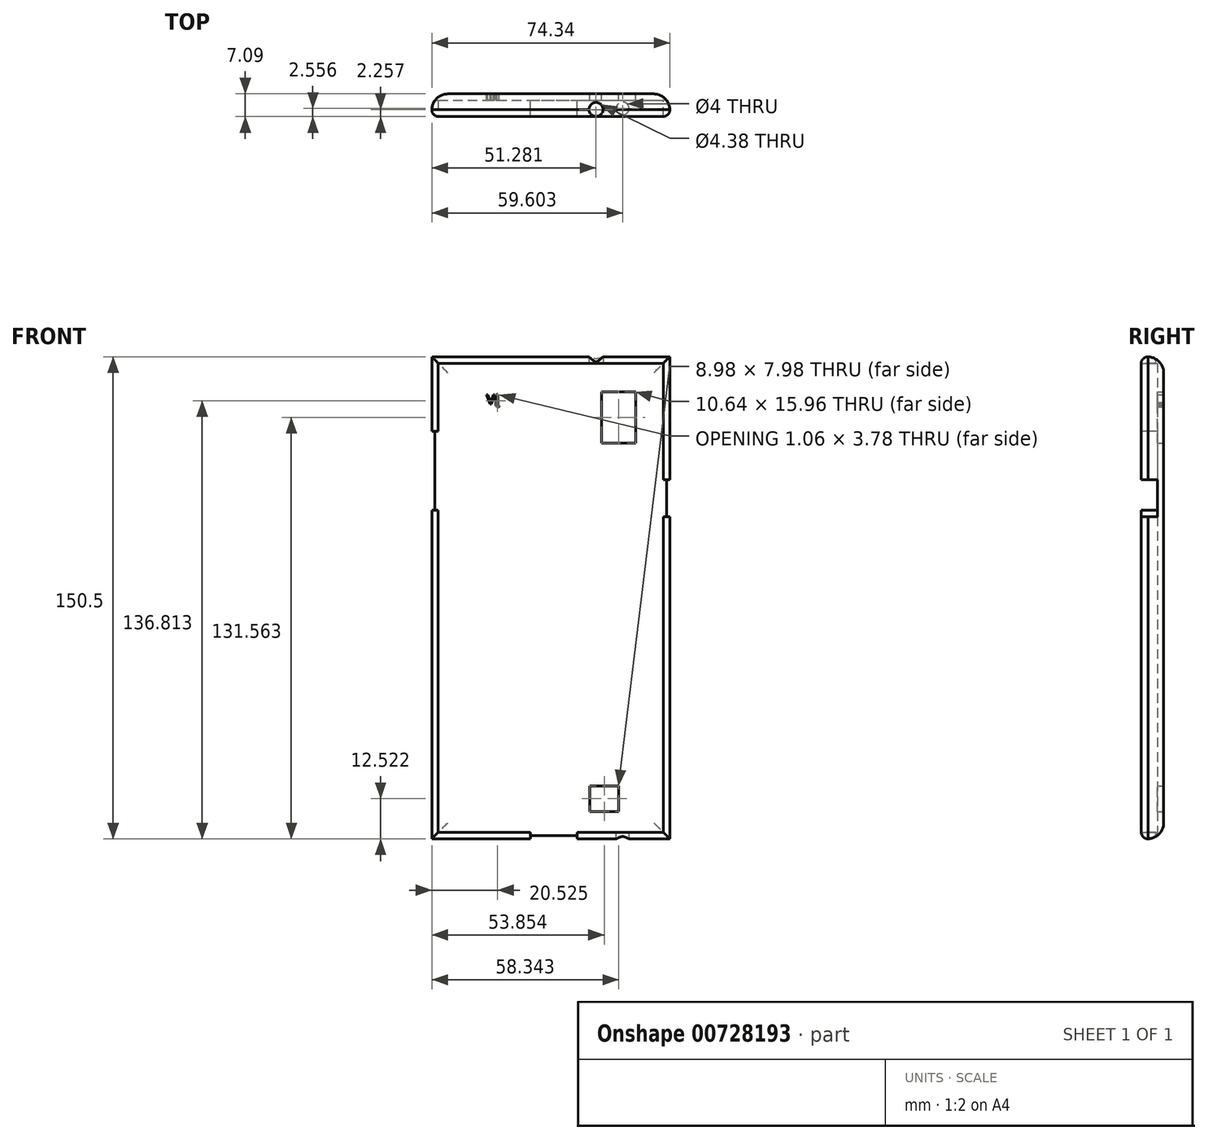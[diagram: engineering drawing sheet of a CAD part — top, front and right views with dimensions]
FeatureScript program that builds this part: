
annotation { "Feature Type Name" : "Feature", "Feature Type Description" : "" }
export const myFeature = defineFeature(function(context is Context, id is Id, definition is map)
    precondition{}
    {
        {
            var Q0;
            Q0=qCreatedBy(makeId("Front.planeOp"),FACE);
            var sketch = newSketch(context, id + "F0", { "sketchPlane" : qUnion([Q0])});
            skLineSegment(sketch, "E0.bottom", {"start": v(-37.17, 75.25) * mm, "end": v(37.17, 75.25) * mm});
            skLineSegment(sketch, "E0.top", {"start": v(-37.17, -75.25) * mm, "end": v(37.17, -75.25) * mm});
            skLineSegment(sketch, "E0.left", {"start": v(-37.17, 75.25) * mm, "end": v(-37.17, -75.25) * mm});
            skLineSegment(sketch, "E0.right", {"start": v(37.17, 75.25) * mm, "end": v(37.17, -75.25) * mm});
            skPoint(sketch, "E0.middle", {"position": v(0, 0) * mm});
            skPoint(sketch, "E1.top.end.orphan", {"position": v(-20.66, 46.9) * mm});
            skPoint(sketch, "E2.left.start.orphan", {"position": v(-20.66, -61.37) * mm});
            skSolve(sketch);
        }
        {
            var Q0;
            Q0 = qSketchRegion(id + "F0", true);
            extrude(context, id + "F1", {"entities" : qUnion([Q0]), "depth" : 7.1 * mm, "offsetDistance" : 25 * mm});
        }
        {
            var Q0;
            Q0=makeQuery(id+"F1.opExtrude","CAP_FACE",FACE,{"disambiguationData":[OSD([sQuery(id+"F0.wireOp",EDGE,"E0.bottom"),sQuery(id+"F0.wireOp",EDGE,"E0.top"),sQuery(id+"F0.wireOp",EDGE,"E0.left"),sQuery(id+"F0.wireOp",EDGE,"E0.right")])],"isStart":false});
            shell(context, id + "F2", {"entities" : qUnion([Q0]), "thickness" : 2 * mm});
        }
        {
            var Q0;
            Q0=makeQuery(id+"F1.opExtrude","CAP_EDGE",EDGE,{"disambiguationData":[OSD([sQuery(id+"F0.wireOp",EDGE,"E0.left")])],"isStart":false});
            var Q1;
            Q1=makeQuery(id+"F1.opExtrude","CAP_EDGE",EDGE,{"disambiguationData":[OSD([sQuery(id+"F0.wireOp",EDGE,"E0.right")])],"isStart":false});
            var Q2;
            Q2=makeQuery(id+"F1.opExtrude","CAP_EDGE",EDGE,{"disambiguationData":[OSD([sQuery(id+"F0.wireOp",EDGE,"E0.top")])],"isStart":false});
            var Q3;
            Q3=makeQuery(id+"F1.opExtrude","CAP_EDGE",EDGE,{"disambiguationData":[OSD([sQuery(id+"F0.wireOp",EDGE,"E0.bottom")])],"isStart":false});
            fillet(context, id + "F3", {"entities" : qUnion([Q0, Q1, Q2, Q3]), "radius" : 2.17 * mm, "tangentPropagation" : true, "allowEdgeOverflow" : false});
        }
        {
            var Q0;
            Q0=makeQuery(id+"F1.opExtrude","CAP_EDGE",EDGE,{"disambiguationData":[OSD([sQuery(id+"F0.wireOp",EDGE,"E0.right")])],"isStart":true});
            var Q1;
            Q1=makeQuery(id+"F1.opExtrude","CAP_EDGE",EDGE,{"disambiguationData":[OSD([sQuery(id+"F0.wireOp",EDGE,"E0.left")])],"isStart":true});
            var Q2;
            Q2=makeQuery(id+"F1.opExtrude","CAP_EDGE",EDGE,{"disambiguationData":[OSD([sQuery(id+"F0.wireOp",EDGE,"E0.top")])],"isStart":true});
            var Q3;
            Q3=makeQuery(id+"F1.opExtrude","CAP_EDGE",EDGE,{"disambiguationData":[OSD([sQuery(id+"F0.wireOp",EDGE,"E0.bottom")])],"isStart":true});
            fillet(context, id + "F4", {"entities" : qUnion([Q0, Q1, Q2, Q3]), "radius" : 5 * mm, "tangentPropagation" : true, "allowEdgeOverflow" : false});
        }
        {
            var Q0;
            Q0=makeQuery(id+"F1.opExtrude","CAP_FACE",FACE,{"disambiguationData":[OSD([sQuery(id+"F0.wireOp",EDGE,"E0.bottom"),sQuery(id+"F0.wireOp",EDGE,"E0.top"),sQuery(id+"F0.wireOp",EDGE,"E0.left"),sQuery(id+"F0.wireOp",EDGE,"E0.right")])],"isStart":true});
            var sketch = newSketch(context, id + "F5", { "sketchPlane" : qUnion([Q0])});
            skLineSegment(sketch, "E3.bottom", {"start": v(-26.5, 64.3) * mm, "end": v(-15.85, 64.3) * mm});
            skLineSegment(sketch, "E3.top", {"start": v(-26.5, 48.33) * mm, "end": v(-15.85, 48.33) * mm});
            skLineSegment(sketch, "E3.left", {"start": v(-26.5, 64.3) * mm, "end": v(-26.5, 48.33) * mm});
            skLineSegment(sketch, "E3.right", {"start": v(-15.85, 64.3) * mm, "end": v(-15.85, 48.33) * mm});
            skLineSegment(sketch, "E4.bottom", {"start": v(-21.17, -58.74) * mm, "end": v(-12.2, -58.74) * mm});
            skLineSegment(sketch, "E4.top", {"start": v(-21.17, -66.72) * mm, "end": v(-12.2, -66.72) * mm});
            skLineSegment(sketch, "E4.left", {"start": v(-21.17, -58.74) * mm, "end": v(-21.17, -66.72) * mm});
            skLineSegment(sketch, "E4.right", {"start": v(-12.2, -58.74) * mm, "end": v(-12.2, -66.72) * mm});
            skSolve(sketch);
        }
        {
            var Q0;
            Q0=makeQuery(id+"F5.imprint","IMPRINT",FACE,{"disambiguationData":[TD([[makeQuery(id+"F5.imprint","IMPRINT",EDGE,{"derivedFrom":sQuery(id+"F5.wireOp",EDGE,"E3.bottom")}),-1.0]])]});
            var Q1;
            Q1=makeQuery(id+"F5.imprint","IMPRINT",FACE,{"disambiguationData":[TD([[makeQuery(id+"F5.imprint","IMPRINT",EDGE,{"derivedFrom":sQuery(id+"F5.wireOp",EDGE,"E4.bottom")}),-1.0]])]});
            extrude(context, id + "F6", {"entities" : qUnion([Q0, Q1]), "operationType" : NewBodyOperationType.REMOVE, "oppositeDirection" : true, "depth" : 25 * mm, "offsetDistance" : 25 * mm});
        }
        {
            var Q0;
            Q0=makeQuery(id+"F2.opShell","OFFSET_FACE",FACE,{"disambiguationData":[OSD([sQuery(id+"F0.wireOp",EDGE,"E0.top")])]});
            var sketch = newSketch(context, id + "F7", { "sketchPlane" : qUnion([Q0])});
            skCircle(sketch, "E5", {"center": v(22.43, -4.53) * mm, "radius": 2 * mm});
            skSolve(sketch);
        }
        {
            var Q0;
            Q0=sQuery(id+"F7.wireOp",VERTEX,"E5.center");
            var Q1;
            Q1=makeQuery(id+"F1.opExtrude","SWEPT_BODY",BODY,{"disambiguationData":[OSD([sQuery(id+"F0.wireOp",EDGE,"E0.bottom"),sQuery(id+"F0.wireOp",EDGE,"E0.top"),sQuery(id+"F0.wireOp",EDGE,"E0.left"),sQuery(id+"F0.wireOp",EDGE,"E0.right")])]});
            hole(context, id + "F8", {"style" : HoleStyle.SIMPLE, "endStyle" : HoleEndStyle.THROUGH, "holeDiameter" : 4 * mm, "majorDiameter" : 5 * mm, "isTappedThrough" : true, "tappedDepth" : 12 * mm, "tapClearance" : 3, "locations" : qUnion([Q0]), "scope" : qUnion([Q1])});
        }
        {
            var Q0;
            Q0=makeQuery(id+"F2.opShell","OFFSET_FACE",FACE,{"disambiguationData":[OSD([sQuery(id+"F0.wireOp",EDGE,"E0.top")])]});
            var sketch = newSketch(context, id + "F9", { "sketchPlane" : qUnion([Q0])});
            skLineSegment(sketch, "E6.bottom", {"start": v(-6.43, -7.1) * mm, "end": v(8.25, -7.1) * mm});
            skLineSegment(sketch, "E6.top", {"start": v(-6.43, -2) * mm, "end": v(8.25, -2) * mm});
            skLineSegment(sketch, "E6.left", {"start": v(-6.43, -7.1) * mm, "end": v(-6.43, -2) * mm});
            skLineSegment(sketch, "E6.right", {"start": v(8.25, -7.1) * mm, "end": v(8.25, -2) * mm});
            skSolve(sketch);
        }
        {
            var Q0;
            Q0 = qSketchRegion(id + "F9", true);
            extrude(context, id + "F10", {"entities" : qUnion([Q0]), "operationType" : NewBodyOperationType.REMOVE, "oppositeDirection" : true, "depth" : 25 * mm, "offsetDistance" : 25 * mm});
        }
        {
            var Q0;
            Q0=makeQuery(id+"F2.opShell","OFFSET_FACE",FACE,{"disambiguationData":[OSD([sQuery(id+"F0.wireOp",EDGE,"E0.bottom")])]});
            var sketch = newSketch(context, id + "F11", { "sketchPlane" : qUnion([Q0])});
            skCircle(sketch, "E7", {"center": v(14.11, 4.83) * mm, "radius": 2.19 * mm});
            skSolve(sketch);
        }
        {
            var Q0;
            Q0 = qSketchRegion(id + "F11", true);
            extrude(context, id + "F12", {"entities" : qUnion([Q0]), "operationType" : NewBodyOperationType.REMOVE, "oppositeDirection" : true, "depth" : 25 * mm, "offsetDistance" : 25 * mm});
        }
        {
            var Q0;
            Q0=makeQuery(id+"F2.opShell","OFFSET_FACE",FACE,{"disambiguationData":[OSD([sQuery(id+"F0.wireOp",EDGE,"E0.left")])]});
            var sketch = newSketch(context, id + "F13", { "sketchPlane" : qUnion([Q0])});
            skLineSegment(sketch, "E8.bottom", {"start": v(-2, 51.96) * mm, "end": v(-7.53, 51.96) * mm});
            skLineSegment(sketch, "E8.top", {"start": v(-2, 27.34) * mm, "end": v(-7.53, 27.34) * mm});
            skLineSegment(sketch, "E8.left", {"start": v(-2, 51.96) * mm, "end": v(-2, 27.34) * mm});
            skLineSegment(sketch, "E8.right", {"start": v(-7.53, 51.96) * mm, "end": v(-7.53, 27.34) * mm});
            skPoint(sketch, "E8.middle", {"position": v(-4.77, 39.65) * mm});
            skSolve(sketch);
        }
        {
            var Q0;
            Q0 = qSketchRegion(id + "F13", true);
            extrude(context, id + "F14", {"entities" : qUnion([Q0]), "operationType" : NewBodyOperationType.REMOVE, "oppositeDirection" : true, "depth" : 22 * mm, "offsetDistance" : 25 * mm});
        }
        {
            var Q0;
            Q0=makeQuery(id+"F2.opShell","OFFSET_FACE",FACE,{"disambiguationData":[OSD([sQuery(id+"F0.wireOp",EDGE,"E0.right")])]});
            var sketch = newSketch(context, id + "F15", { "sketchPlane" : qUnion([Q0])});
            skLineSegment(sketch, "E9.bottom", {"start": v(7.1, 36.84) * mm, "end": v(2, 36.84) * mm});
            skLineSegment(sketch, "E9.top", {"start": v(7.1, 25.38) * mm, "end": v(2, 25.38) * mm});
            skLineSegment(sketch, "E9.left", {"start": v(7.1, 36.84) * mm, "end": v(7.1, 25.38) * mm});
            skLineSegment(sketch, "E9.right", {"start": v(2, 36.84) * mm, "end": v(2, 25.38) * mm});
            skSolve(sketch);
        }
        {
            var Q0;
            Q0 = qSketchRegion(id + "F15", true);
            extrude(context, id + "F16", {"entities" : qUnion([Q0]), "operationType" : NewBodyOperationType.REMOVE, "oppositeDirection" : true, "depth" : 25 * mm, "offsetDistance" : 25 * mm});
        }
        {
            var Q0;
            Q0=makeQuery(id+"F1.opExtrude","CAP_FACE",FACE,{"disambiguationData":[OSD([sQuery(id+"F0.wireOp",EDGE,"E0.bottom"),sQuery(id+"F0.wireOp",EDGE,"E0.top"),sQuery(id+"F0.wireOp",EDGE,"E0.left"),sQuery(id+"F0.wireOp",EDGE,"E0.right")])],"isStart":true});
            var sketch = newSketch(context, id + "F17", { "sketchPlane" : qUnion([Q0])});
            skText(sketch, "E10", { "text": "JV", "fontName": "OpenSans-Regular.ttf"});
            const initialGuessF17  = {"E10": [0.01644, 0.06046, 1, 0, 0.00302]};
            skSetInitialGuess(sketch, initialGuessF17);
            skSolve(sketch);
        }
        {
            var Q0;
            Q0 = qSketchRegion(id + "F17", true);
            extrude(context, id + "F18", {"entities" : qUnion([Q0]), "operationType" : NewBodyOperationType.REMOVE, "oppositeDirection" : true, "depth" : 25 * mm, "offsetDistance" : 25 * mm});
        }
    });
